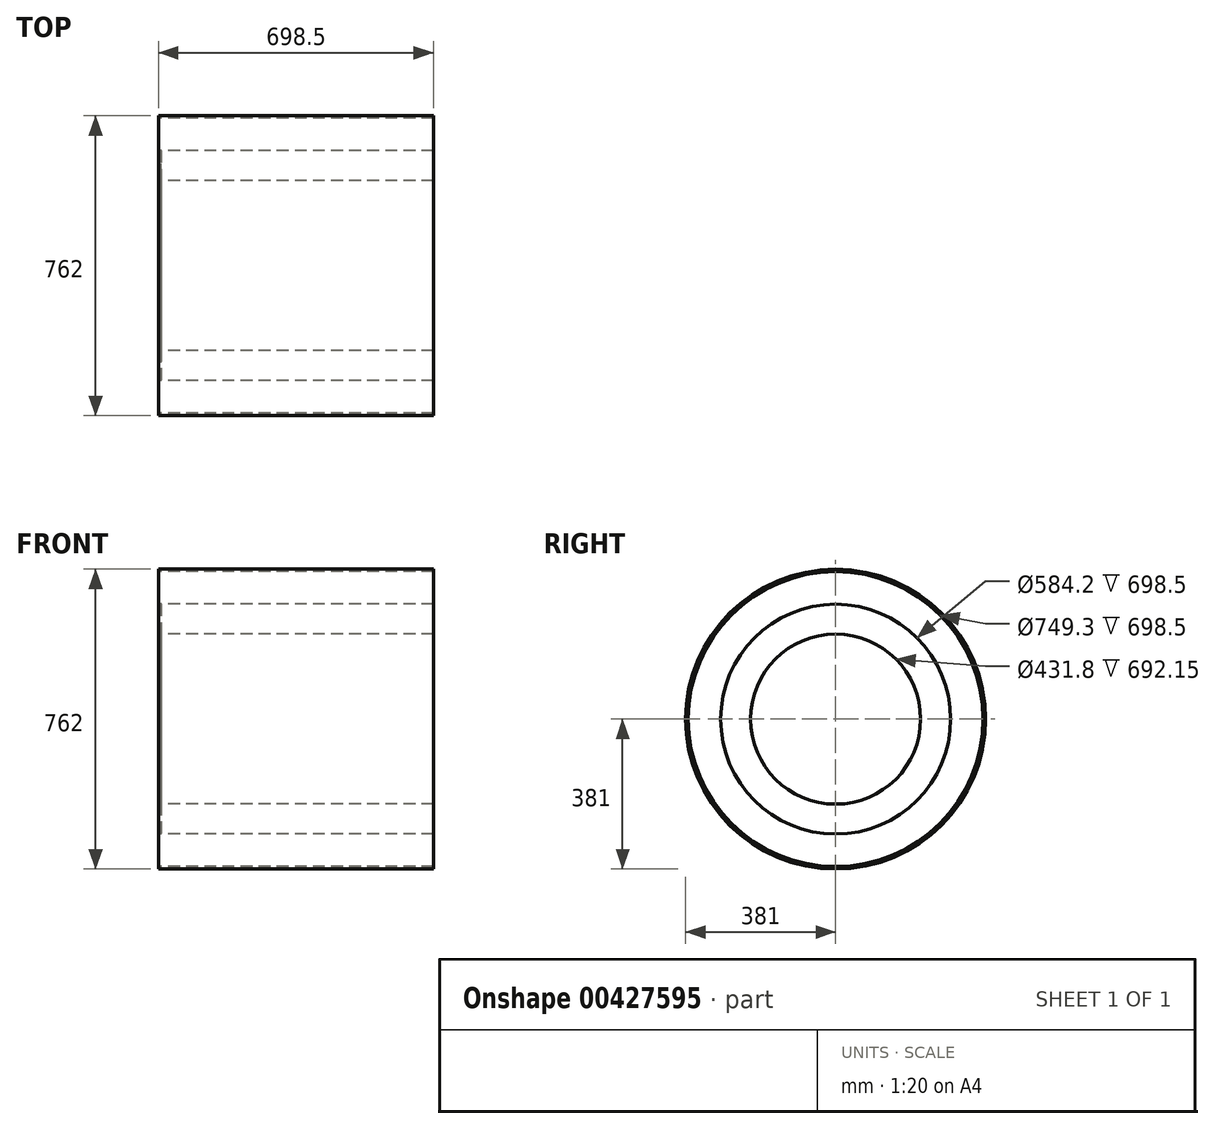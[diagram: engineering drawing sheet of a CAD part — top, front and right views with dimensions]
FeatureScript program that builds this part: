
annotation { "Feature Type Name" : "Feature", "Feature Type Description" : "" }
export const myFeature = defineFeature(function(context is Context, id is Id, definition is map)
    precondition{}
    {
        {
            var Q0;
            Q0=qCreatedBy(makeId("Front.planeOp"),FACE);
            var sketch = newSketch(context, id + "F0", { "sketchPlane" : qUnion([Q0])});
            skLineSegment(sketch, "E0", {"start": v(-349.25, 0) * mm, "end": v(349.25, 0) * mm, "construction": true});
            skLineSegment(sketch, "E1", {"start": v(-349.25, 381) * mm, "end": v(349.25, 381) * mm});
            skLineSegment(sketch, "E2.0", {"start": v(-349.25, 374.65) * mm, "end": v(349.25, 374.65) * mm});
            skLineSegment(sketch, "E3", {"start": v(349.25, 381) * mm, "end": v(349.25, 374.65) * mm});
            skLineSegment(sketch, "E4", {"start": v(-349.25, 381) * mm, "end": v(-349.25, 374.65) * mm});
            skLineSegment(sketch, "E5", {"start": v(-349.25, 374.65) * mm, "end": v(-349.25, 292.1) * mm});
            skLineSegment(sketch, "E6", {"start": v(-349.25, 292.1) * mm, "end": v(349.25, 292.1) * mm});
            skLineSegment(sketch, "E7", {"start": v(349.25, 292.1) * mm, "end": v(349.25, 374.65) * mm});
            skLineSegment(sketch, "E8", {"start": v(-349.25, 292.1) * mm, "end": v(-349.25, 215.9) * mm});
            skLineSegment(sketch, "E9", {"start": v(-349.25, 215.9) * mm, "end": v(349.25, 215.9) * mm});
            skLineSegment(sketch, "E10", {"start": v(349.25, 215.9) * mm, "end": v(349.25, 292.1) * mm});
            skSolve(sketch);
        }
        {
            var Q0;
            Q0=makeQuery(id+"F0.imprint","IMPRINT",FACE,{"disambiguationData":[TD([[makeQuery(id+"F0.imprint","IMPRINT",EDGE,{"derivedFrom":sQuery(id+"F0.wireOp",EDGE,"E6")}),-1.0]])]});
            var Q1;
            Q1=sQuery(id+"F0.wireOp",EDGE,"E0");
            revolve(context, id + "F1", {"entities" : qUnion([Q0]), "axis" : qUnion([Q1]), "revolveType" : RevolveType.FULL});
        }
        {
            var Q0;
            Q0=makeQuery(id+"F0.imprint","IMPRINT",FACE,{"disambiguationData":[TD([[makeQuery(id+"F0.imprint","IMPRINT",EDGE,{"derivedFrom":sQuery(id+"F0.wireOp",EDGE,"E2.0")}),-1.0]])]});
            var Q1;
            Q1=sQuery(id+"F0.wireOp",EDGE,"E0");
            revolve(context, id + "F2", {"entities" : qUnion([Q0]), "axis" : qUnion([Q1]), "revolveType" : RevolveType.FULL});
        }
        {
            var Q0;
            Q0=makeQuery(id+"F0.imprint","IMPRINT",FACE,{"disambiguationData":[TD([[makeQuery(id+"F0.imprint","IMPRINT",EDGE,{"derivedFrom":sQuery(id+"F0.wireOp",EDGE,"E1")}),-1.0]])]});
            var Q1;
            Q1=sQuery(id+"F0.wireOp",EDGE,"E0");
            revolve(context, id + "F3", {"entities" : qUnion([Q0]), "axis" : qUnion([Q1]), "revolveType" : RevolveType.FULL});
        }
        {
            var Q0;
            Q0=makeQuery(id+"F1.opRevolve","SWEPT_FACE",FACE,{"disambiguationData":[OSD([sQuery(id+"F0.wireOp",EDGE,"E8")])]});
            extrude(context, id + "F4", {"entities" : qUnion([Q0]), "operationType" : NewBodyOperationType.REMOVE, "oppositeDirection" : true, "depth" : 6.35 * mm});
        }
    });
